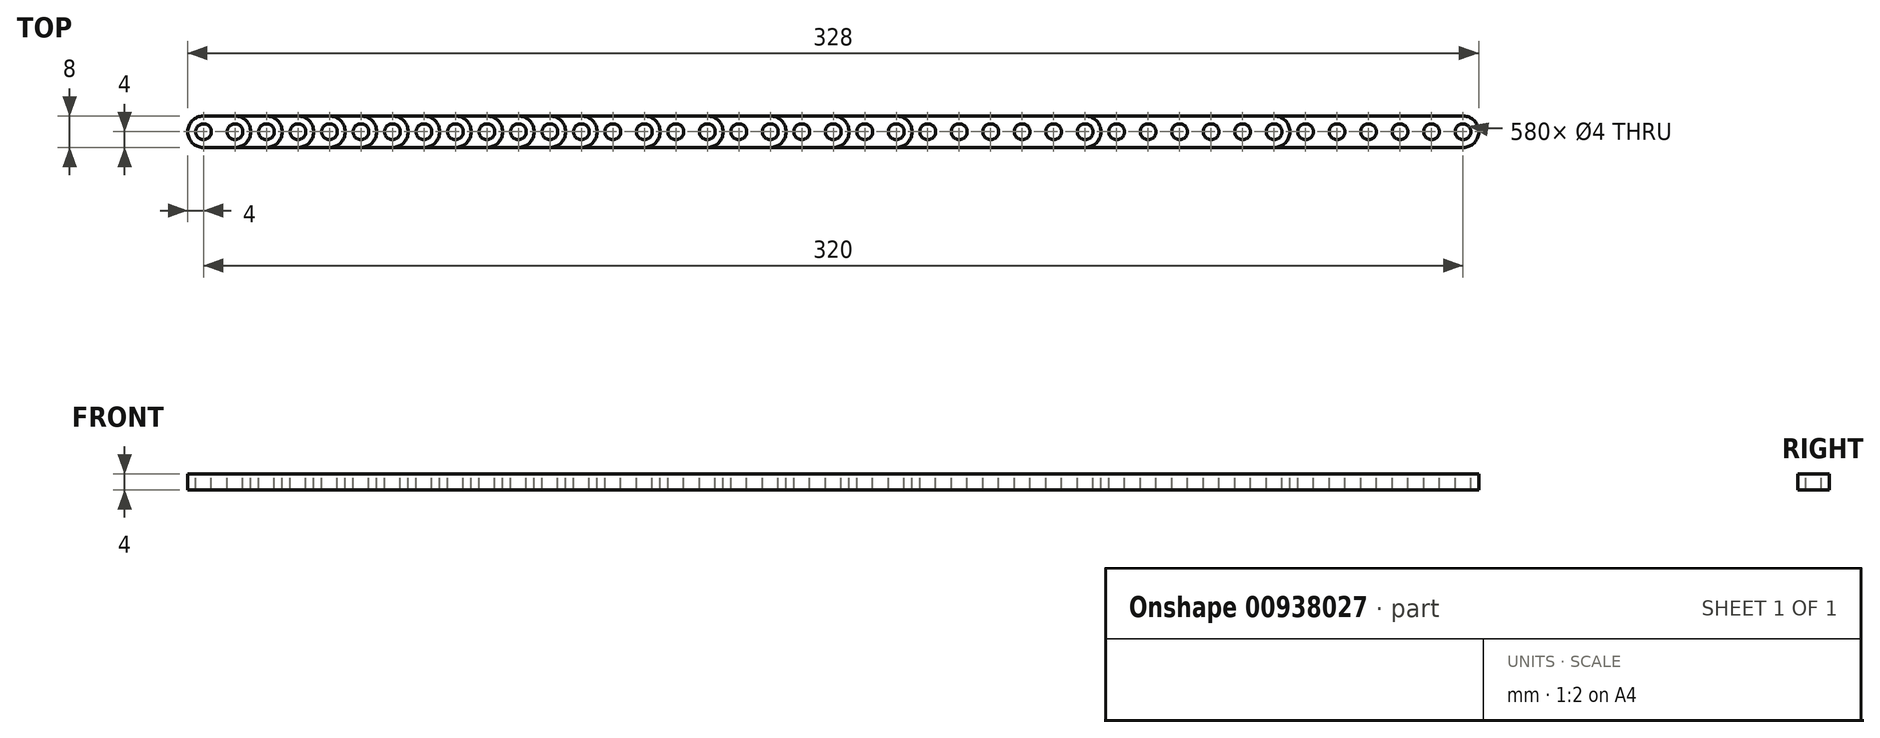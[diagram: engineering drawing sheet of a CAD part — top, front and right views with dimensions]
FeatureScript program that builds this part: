
annotation { "Feature Type Name" : "Feature", "Feature Type Description" : "" }
export const myFeature = defineFeature(function(context is Context, id is Id, definition is map)
    precondition{}
    {
        {
            var Q0;
            Q0=qCreatedBy(makeId("Right.planeOp"),FACE);
            var sketch = newSketch(context, id + "F0", { "sketchPlane" : qUnion([Q0]) });
            skLineSegment(sketch, "E0.bottom", {"start": v(4, 2) * mm, "end": v(-4, 2) * mm});
            skLineSegment(sketch, "E0.top", {"start": v(4, -2) * mm, "end": v(-4, -2) * mm});
            skLineSegment(sketch, "E0.left", {"start": v(4, 2) * mm, "end": v(4, -2) * mm});
            skLineSegment(sketch, "E0.right", {"start": v(-4, 2) * mm, "end": v(-4, -2) * mm});
            skPoint(sketch, "E0.middle", {"position": v(0, 0) * mm});
            skSolve(sketch);
        }
        {
            var Q0;
            Q0=qSketchRegion(id+"F0",true);
            extrude(context, id + "F1", {"entities" : qUnion([Q0]), "depth" : 16 * mm, "offsetDistance" : 25 * mm});
        }
        {
            var Q0;
            Q0=qSketchRegion(id+"F0",true);
            extrude(context, id + "F2", {"entities" : qUnion([Q0]), "depth" : 24 * mm, "offsetDistance" : 25 * mm});
        }
        {
            var Q0;
            Q0=qSketchRegion(id+"F0",true);
            extrude(context, id + "F3", {"entities" : qUnion([Q0]), "depth" : 32 * mm, "offsetDistance" : 25 * mm});
        }
        {
            var Q0;
            Q0=qSketchRegion(id+"F0",true);
            extrude(context, id + "F4", {"entities" : qUnion([Q0]), "depth" : 40 * mm, "offsetDistance" : 25 * mm});
        }
        {
            var Q0;
            Q0=qSketchRegion(id+"F0",true);
            extrude(context, id + "F5", {"entities" : qUnion([Q0]), "depth" : 48 * mm, "offsetDistance" : 25 * mm});
        }
        {
            var Q0;
            Q0=qSketchRegion(id+"F0",true);
            extrude(context, id + "F6", {"entities" : qUnion([Q0]), "depth" : 56 * mm, "offsetDistance" : 25 * mm});
        }
        {
            var Q0;
            Q0=qSketchRegion(id+"F0",true);
            extrude(context, id + "F7", {"entities" : qUnion([Q0]), "depth" : 64 * mm, "offsetDistance" : 25 * mm});
        }
        {
            var Q0;
            Q0=qSketchRegion(id+"F0",true);
            extrude(context, id + "F8", {"entities" : qUnion([Q0]), "depth" : 72 * mm, "offsetDistance" : 25 * mm});
        }
        {
            var Q0;
            Q0=qSketchRegion(id+"F0",true);
            extrude(context, id + "F9", {"entities" : qUnion([Q0]), "depth" : 80 * mm, "offsetDistance" : 25 * mm});
        }
        {
            var Q0;
            Q0=qSketchRegion(id+"F0",true);
            extrude(context, id + "F10", {"entities" : qUnion([Q0]), "depth" : 88 * mm, "offsetDistance" : 25 * mm});
        }
        {
            var Q0;
            Q0=qSketchRegion(id+"F0",true);
            extrude(context, id + "F11", {"entities" : qUnion([Q0]), "depth" : 96 * mm, "offsetDistance" : 25 * mm});
        }
        {
            var Q0;
            Q0=qSketchRegion(id+"F0",true);
            extrude(context, id + "F12", {"entities" : qUnion([Q0]), "depth" : 104 * mm, "offsetDistance" : 25 * mm});
        }
        {
            var Q0;
            Q0=qSketchRegion(id+"F0",true);
            extrude(context, id + "F13", {"entities" : qUnion([Q0]), "depth" : 120 * mm, "offsetDistance" : 25 * mm});
        }
        {
            var Q0;
            Q0=qSketchRegion(id+"F0",true);
            extrude(context, id + "F14", {"entities" : qUnion([Q0]), "depth" : 136 * mm, "offsetDistance" : 25 * mm});
        }
        {
            var Q0;
            Q0=qSketchRegion(id+"F0",true);
            extrude(context, id + "F15", {"entities" : qUnion([Q0]), "depth" : 152 * mm, "offsetDistance" : 25 * mm});
        }
        {
            var Q0;
            Q0=qSketchRegion(id+"F0",true);
            extrude(context, id + "F16", {"entities" : qUnion([Q0]), "depth" : 168 * mm, "offsetDistance" : 25 * mm});
        }
        {
            var Q0;
            Q0=qSketchRegion(id+"F0",true);
            extrude(context, id + "F17", {"entities" : qUnion([Q0]), "depth" : 184 * mm, "offsetDistance" : 25 * mm});
        }
        {
            var Q0;
            Q0=qSketchRegion(id+"F0",true);
            extrude(context, id + "F18", {"entities" : qUnion([Q0]), "depth" : 232 * mm, "offsetDistance" : 25 * mm});
        }
        {
            var Q0;
            Q0=qSketchRegion(id+"F0",true);
            extrude(context, id + "F19", {"entities" : qUnion([Q0]), "depth" : 280 * mm, "offsetDistance" : 25 * mm});
        }
        {
            var Q0;
            Q0=qSketchRegion(id+"F0",true);
            extrude(context, id + "F20", {"entities" : qUnion([Q0]), "depth" : 328 * mm, "offsetDistance" : 25 * mm});
        }
        {
            var Q0;
            Q0=qCreatedBy(makeId("Top.planeOp"),FACE);
            var sketch = newSketch(context, id + "F21", { "sketchPlane" : qUnion([Q0]) });
            skCircle(sketch, "E1", {"center": v(4, 0) * mm, "radius": 2 * mm});
            skCircle(sketch, "E2.1.0.0", {"center": v(12, 0) * mm, "radius": 2 * mm});
            skCircle(sketch, "E2.2.0.0", {"center": v(20, 0) * mm, "radius": 2 * mm});
            skCircle(sketch, "E2.3.0.0", {"center": v(28, 0) * mm, "radius": 2 * mm});
            skCircle(sketch, "E2.4.0.0", {"center": v(36, 0) * mm, "radius": 2 * mm});
            skCircle(sketch, "E2.5.0.0", {"center": v(44, 0) * mm, "radius": 2 * mm});
            skCircle(sketch, "E2.6.0.0", {"center": v(52, 0) * mm, "radius": 2 * mm});
            skCircle(sketch, "E2.7.0.0", {"center": v(60, 0) * mm, "radius": 2 * mm});
            skCircle(sketch, "E2.8.0.0", {"center": v(68, 0) * mm, "radius": 2 * mm});
            skCircle(sketch, "E2.9.0.0", {"center": v(76, 0) * mm, "radius": 2 * mm});
            skCircle(sketch, "E2.10.0.0", {"center": v(84, 0) * mm, "radius": 2 * mm});
            skCircle(sketch, "E2.11.0.0", {"center": v(92, 0) * mm, "radius": 2 * mm});
            skCircle(sketch, "E2.12.0.0", {"center": v(100, 0) * mm, "radius": 2 * mm});
            skCircle(sketch, "E2.13.0.0", {"center": v(108, 0) * mm, "radius": 2 * mm});
            skCircle(sketch, "E2.14.0.0", {"center": v(116, 0) * mm, "radius": 2 * mm});
            skCircle(sketch, "E2.15.0.0", {"center": v(124, 0) * mm, "radius": 2 * mm});
            skCircle(sketch, "E2.16.0.0", {"center": v(132, 0) * mm, "radius": 2 * mm});
            skCircle(sketch, "E2.17.0.0", {"center": v(140, 0) * mm, "radius": 2 * mm});
            skCircle(sketch, "E2.18.0.0", {"center": v(148, 0) * mm, "radius": 2 * mm});
            skCircle(sketch, "E2.19.0.0", {"center": v(156, 0) * mm, "radius": 2 * mm});
            skCircle(sketch, "E2.20.0.0", {"center": v(164, 0) * mm, "radius": 2 * mm});
            skCircle(sketch, "E2.21.0.0", {"center": v(172, 0) * mm, "radius": 2 * mm});
            skCircle(sketch, "E2.22.0.0", {"center": v(180, 0) * mm, "radius": 2 * mm});
            skCircle(sketch, "E2.23.0.0", {"center": v(188, 0) * mm, "radius": 2 * mm});
            skCircle(sketch, "E2.24.0.0", {"center": v(196, 0) * mm, "radius": 2 * mm});
            skCircle(sketch, "E2.25.0.0", {"center": v(204, 0) * mm, "radius": 2 * mm});
            skCircle(sketch, "E2.26.0.0", {"center": v(212, 0) * mm, "radius": 2 * mm});
            skCircle(sketch, "E2.27.0.0", {"center": v(220, 0) * mm, "radius": 2 * mm});
            skCircle(sketch, "E2.28.0.0", {"center": v(228, 0) * mm, "radius": 2 * mm});
            skCircle(sketch, "E2.29.0.0", {"center": v(236, 0) * mm, "radius": 2 * mm});
            skCircle(sketch, "E2.30.0.0", {"center": v(244, 0) * mm, "radius": 2 * mm});
            skCircle(sketch, "E2.31.0.0", {"center": v(252, 0) * mm, "radius": 2 * mm});
            skCircle(sketch, "E2.32.0.0", {"center": v(260, 0) * mm, "radius": 2 * mm});
            skCircle(sketch, "E2.33.0.0", {"center": v(268, 0) * mm, "radius": 2 * mm});
            skCircle(sketch, "E2.34.0.0", {"center": v(276, 0) * mm, "radius": 2 * mm});
            skCircle(sketch, "E2.35.0.0", {"center": v(284, 0) * mm, "radius": 2 * mm});
            skCircle(sketch, "E2.36.0.0", {"center": v(292, 0) * mm, "radius": 2 * mm});
            skCircle(sketch, "E2.37.0.0", {"center": v(300, 0) * mm, "radius": 2 * mm});
            skCircle(sketch, "E2.38.0.0", {"center": v(308, 0) * mm, "radius": 2 * mm});
            skCircle(sketch, "E2.39.0.0", {"center": v(316, 0) * mm, "radius": 2 * mm});
            skCircle(sketch, "E2.40.0.0", {"center": v(324, 0) * mm, "radius": 2 * mm});
            skLineSegment(sketch, "E2.direction1", {"start": v(4, 0) * mm, "end": v(12, 0) * mm, "construction": true});
            skLineSegment(sketch, "E3.0", {"start": v(0, 4) * mm, "end": v(0, -4) * mm});
            skLineSegment(sketch, "E4.0", {"start": v(4, -4) * mm, "end": v(0, -4) * mm, "construction": true});
            skLineSegment(sketch, "E5.0", {"start": v(4, 4) * mm, "end": v(0, 4) * mm, "construction": true});
            skArc(sketch, "E6", {"start": v(4, -4) * mm, "mid": v(0, 0) * mm, "end": v(4, 4) * mm});
            skPoint(sketch, "E7.orphan", {"position": v(16, -4) * mm});
            skPoint(sketch, "E8.orphan", {"position": v(16, 4) * mm});
            skLineSegment(sketch, "E9", {"start": v(0, -4) * mm, "end": v(4, -4) * mm});
            skLineSegment(sketch, "E10", {"start": v(0, 4) * mm, "end": v(4, 4) * mm});
            skSolve(sketch);
        }
        {
            var Q0;
            Q0=qSketchRegion(id+"F21",true);
            extrude(context, id + "F22", {"entities" : qUnion([Q0]), "operationType" : NewBodyOperationType.REMOVE, "endBound" : BoundingType.SYMMETRIC, "oppositeDirection" : true, "depth" : 25 * mm, "offsetDistance" : 25 * mm});
        }
        {
            var Q0;
            Q0=makeQuery(id+"F20.opExtrude","CAP_EDGE",EDGE,{"disambiguationData":[OSD([sQuery(id+"F0.wireOp",EDGE,"E0.right")])],"isStart":false});
            var Q1;
            Q1=makeQuery(id+"F20.opExtrude","CAP_EDGE",EDGE,{"disambiguationData":[OSD([sQuery(id+"F0.wireOp",EDGE,"E0.left")])],"isStart":false});
            var Q2;
            Q2=makeQuery(id+"F19.opExtrude","CAP_EDGE",EDGE,{"disambiguationData":[OSD([sQuery(id+"F0.wireOp",EDGE,"E0.right")])],"isStart":false});
            var Q3;
            Q3=makeQuery(id+"F19.opExtrude","CAP_EDGE",EDGE,{"disambiguationData":[OSD([sQuery(id+"F0.wireOp",EDGE,"E0.left")])],"isStart":false});
            var Q4;
            Q4=makeQuery(id+"F18.opExtrude","CAP_EDGE",EDGE,{"disambiguationData":[OSD([sQuery(id+"F0.wireOp",EDGE,"E0.right")])],"isStart":false});
            var Q5;
            Q5=makeQuery(id+"F17.opExtrude","CAP_EDGE",EDGE,{"disambiguationData":[OSD([sQuery(id+"F0.wireOp",EDGE,"E0.right")])],"isStart":false});
            var Q6;
            Q6=makeQuery(id+"F16.opExtrude","CAP_EDGE",EDGE,{"disambiguationData":[OSD([sQuery(id+"F0.wireOp",EDGE,"E0.right")])],"isStart":false});
            var Q7;
            Q7=makeQuery(id+"F15.opExtrude","CAP_EDGE",EDGE,{"disambiguationData":[OSD([sQuery(id+"F0.wireOp",EDGE,"E0.right")])],"isStart":false});
            var Q8;
            Q8=makeQuery(id+"F14.opExtrude","CAP_EDGE",EDGE,{"disambiguationData":[OSD([sQuery(id+"F0.wireOp",EDGE,"E0.right")])],"isStart":false});
            var Q9;
            Q9=makeQuery(id+"F13.opExtrude","CAP_EDGE",EDGE,{"disambiguationData":[OSD([sQuery(id+"F0.wireOp",EDGE,"E0.right")])],"isStart":false});
            var Q10;
            Q10=makeQuery(id+"F12.opExtrude","CAP_EDGE",EDGE,{"disambiguationData":[OSD([sQuery(id+"F0.wireOp",EDGE,"E0.right")])],"isStart":false});
            var Q11;
            Q11=makeQuery(id+"F11.opExtrude","CAP_EDGE",EDGE,{"disambiguationData":[OSD([sQuery(id+"F0.wireOp",EDGE,"E0.right")])],"isStart":false});
            var Q12;
            Q12=makeQuery(id+"F10.opExtrude","CAP_EDGE",EDGE,{"disambiguationData":[OSD([sQuery(id+"F0.wireOp",EDGE,"E0.right")])],"isStart":false});
            var Q13;
            Q13=makeQuery(id+"F9.opExtrude","CAP_EDGE",EDGE,{"disambiguationData":[OSD([sQuery(id+"F0.wireOp",EDGE,"E0.right")])],"isStart":false});
            var Q14;
            Q14=makeQuery(id+"F8.opExtrude","CAP_EDGE",EDGE,{"disambiguationData":[OSD([sQuery(id+"F0.wireOp",EDGE,"E0.right")])],"isStart":false});
            var Q15;
            Q15=makeQuery(id+"F7.opExtrude","CAP_EDGE",EDGE,{"disambiguationData":[OSD([sQuery(id+"F0.wireOp",EDGE,"E0.right")])],"isStart":false});
            var Q16;
            Q16=makeQuery(id+"F6.opExtrude","CAP_EDGE",EDGE,{"disambiguationData":[OSD([sQuery(id+"F0.wireOp",EDGE,"E0.right")])],"isStart":false});
            var Q17;
            Q17=makeQuery(id+"F5.opExtrude","CAP_EDGE",EDGE,{"disambiguationData":[OSD([sQuery(id+"F0.wireOp",EDGE,"E0.right")])],"isStart":false});
            var Q18;
            Q18=makeQuery(id+"F4.opExtrude","CAP_EDGE",EDGE,{"disambiguationData":[OSD([sQuery(id+"F0.wireOp",EDGE,"E0.right")])],"isStart":false});
            var Q19;
            Q19=makeQuery(id+"F3.opExtrude","CAP_EDGE",EDGE,{"disambiguationData":[OSD([sQuery(id+"F0.wireOp",EDGE,"E0.right")])],"isStart":false});
            var Q20;
            Q20=makeQuery(id+"F2.opExtrude","CAP_EDGE",EDGE,{"disambiguationData":[OSD([sQuery(id+"F0.wireOp",EDGE,"E0.right")])],"isStart":false});
            var Q21;
            Q21=makeQuery(id+"F1.opExtrude","CAP_EDGE",EDGE,{"disambiguationData":[OSD([sQuery(id+"F0.wireOp",EDGE,"E0.right")])],"isStart":false});
            var Q22;
            Q22=makeQuery(id+"F18.opExtrude","CAP_EDGE",EDGE,{"disambiguationData":[OSD([sQuery(id+"F0.wireOp",EDGE,"E0.left")])],"isStart":false});
            var Q23;
            Q23=makeQuery(id+"F17.opExtrude","CAP_EDGE",EDGE,{"disambiguationData":[OSD([sQuery(id+"F0.wireOp",EDGE,"E0.left")])],"isStart":false});
            var Q24;
            Q24=makeQuery(id+"F16.opExtrude","CAP_EDGE",EDGE,{"disambiguationData":[OSD([sQuery(id+"F0.wireOp",EDGE,"E0.left")])],"isStart":false});
            var Q25;
            Q25=makeQuery(id+"F15.opExtrude","CAP_EDGE",EDGE,{"disambiguationData":[OSD([sQuery(id+"F0.wireOp",EDGE,"E0.left")])],"isStart":false});
            var Q26;
            Q26=makeQuery(id+"F14.opExtrude","CAP_EDGE",EDGE,{"disambiguationData":[OSD([sQuery(id+"F0.wireOp",EDGE,"E0.left")])],"isStart":false});
            var Q27;
            Q27=makeQuery(id+"F13.opExtrude","CAP_EDGE",EDGE,{"disambiguationData":[OSD([sQuery(id+"F0.wireOp",EDGE,"E0.left")])],"isStart":false});
            var Q28;
            Q28=makeQuery(id+"F12.opExtrude","CAP_EDGE",EDGE,{"disambiguationData":[OSD([sQuery(id+"F0.wireOp",EDGE,"E0.left")])],"isStart":false});
            var Q29;
            Q29=makeQuery(id+"F11.opExtrude","CAP_EDGE",EDGE,{"disambiguationData":[OSD([sQuery(id+"F0.wireOp",EDGE,"E0.left")])],"isStart":false});
            var Q30;
            Q30=makeQuery(id+"F10.opExtrude","CAP_EDGE",EDGE,{"disambiguationData":[OSD([sQuery(id+"F0.wireOp",EDGE,"E0.left")])],"isStart":false});
            var Q31;
            Q31=makeQuery(id+"F9.opExtrude","CAP_EDGE",EDGE,{"disambiguationData":[OSD([sQuery(id+"F0.wireOp",EDGE,"E0.left")])],"isStart":false});
            var Q32;
            Q32=makeQuery(id+"F8.opExtrude","CAP_EDGE",EDGE,{"disambiguationData":[OSD([sQuery(id+"F0.wireOp",EDGE,"E0.left")])],"isStart":false});
            var Q33;
            Q33=makeQuery(id+"F7.opExtrude","CAP_EDGE",EDGE,{"disambiguationData":[OSD([sQuery(id+"F0.wireOp",EDGE,"E0.left")])],"isStart":false});
            var Q34;
            Q34=makeQuery(id+"F6.opExtrude","CAP_EDGE",EDGE,{"disambiguationData":[OSD([sQuery(id+"F0.wireOp",EDGE,"E0.left")])],"isStart":false});
            var Q35;
            Q35=makeQuery(id+"F5.opExtrude","CAP_EDGE",EDGE,{"disambiguationData":[OSD([sQuery(id+"F0.wireOp",EDGE,"E0.left")])],"isStart":false});
            var Q36;
            Q36=makeQuery(id+"F4.opExtrude","CAP_EDGE",EDGE,{"disambiguationData":[OSD([sQuery(id+"F0.wireOp",EDGE,"E0.left")])],"isStart":false});
            var Q37;
            Q37=makeQuery(id+"F3.opExtrude","CAP_EDGE",EDGE,{"disambiguationData":[OSD([sQuery(id+"F0.wireOp",EDGE,"E0.left")])],"isStart":false});
            var Q38;
            Q38=makeQuery(id+"F2.opExtrude","CAP_EDGE",EDGE,{"disambiguationData":[OSD([sQuery(id+"F0.wireOp",EDGE,"E0.left")])],"isStart":false});
            var Q39;
            Q39=makeQuery(id+"F1.opExtrude","CAP_EDGE",EDGE,{"disambiguationData":[OSD([sQuery(id+"F0.wireOp",EDGE,"E0.left")])],"isStart":false});
            fillet(context, id + "F23", {"entities" : qUnion([Q0, Q1, Q2, Q3, Q4, Q5, Q6, Q7, Q8, Q9, Q10, Q11, Q12, Q13, Q14, Q15, Q16, Q17, Q18, Q19, Q20, Q21, Q22, Q23, Q24, Q25, Q26, Q27, Q28, Q29, Q30, Q31, Q32, Q33, Q34, Q35, Q36, Q37, Q38, Q39]), "radius" : 4 * mm, "tangentPropagation" : true, "conicFillet" : false});
        }
    });
